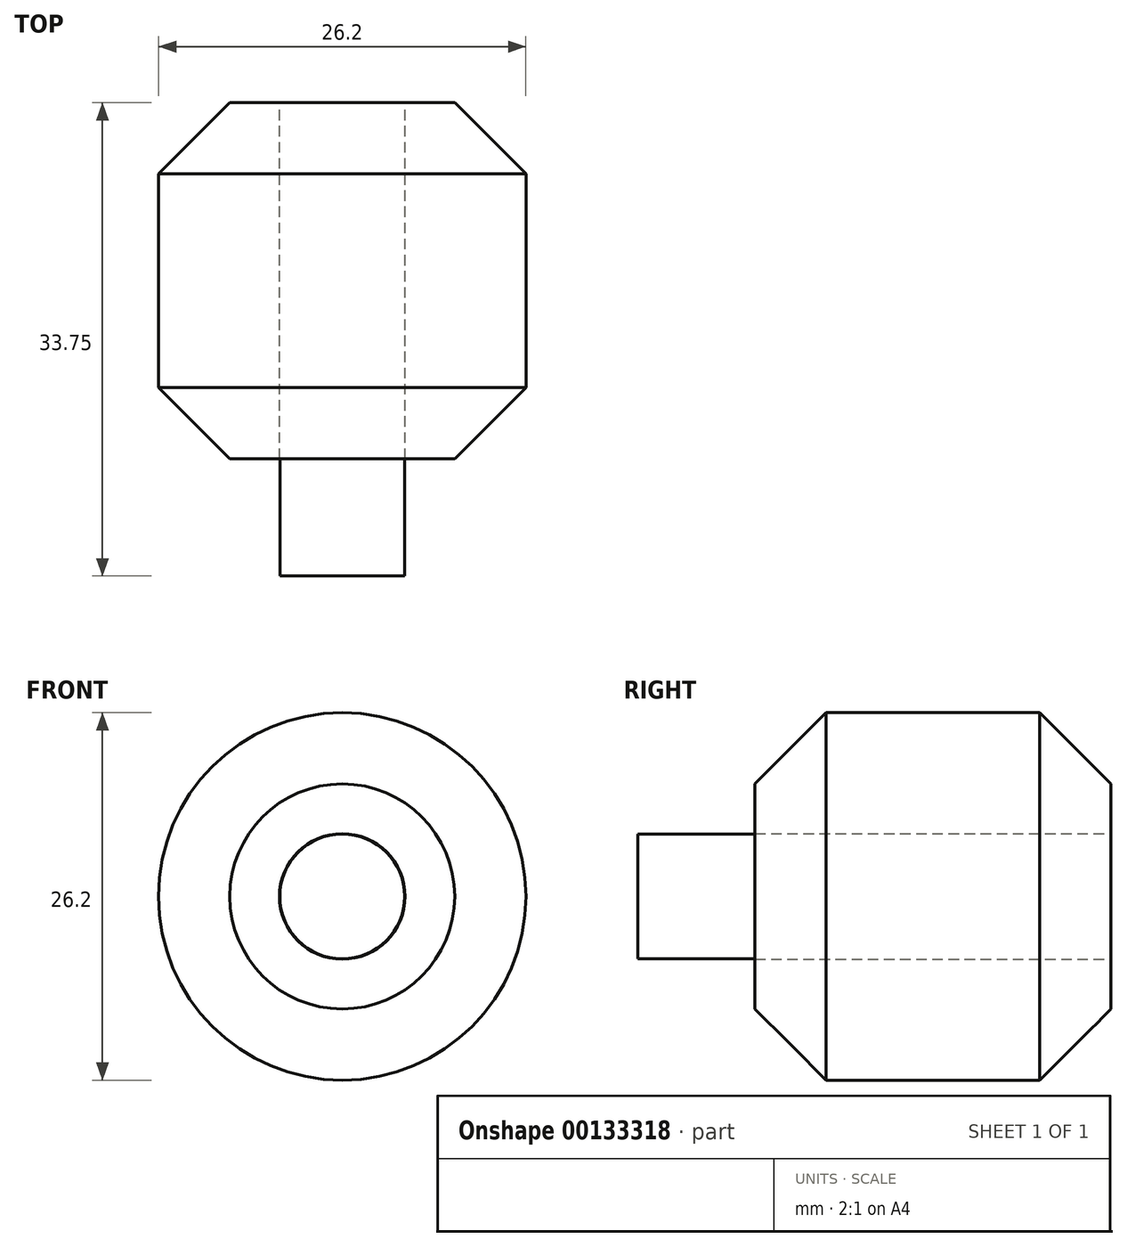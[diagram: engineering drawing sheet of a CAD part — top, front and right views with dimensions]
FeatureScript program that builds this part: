
annotation { "Feature Type Name" : "Feature", "Feature Type Description" : "" }
export const myFeature = defineFeature(function(context is Context, id is Id, definition is map)
    precondition{}
    {
        {
            var Q0;
            Q0=qCreatedBy(makeId("Front.planeOp"),FACE);
            var sketch = newSketch(context, id + "F0", { "sketchPlane" : qUnion([Q0])});
            skCircle(sketch, "E0", {"center": v(0, 0) * mm, "radius": 13.1 * mm});
            skCircle(sketch, "E1", {"center": v(0, 0) * mm, "radius": 4.48 * mm});
            skSolve(sketch);
        }
        {
            var Q0;
            Q0 = qSketchRegion(id + "F0", true);
            extrude(context, id + "F1", {"entities" : qUnion([Q0]), "depth" : 25.4 * mm});
        }
        {
            var Q0;
            Q0=makeQuery(id+"F1.opExtrude","CAP_FACE",FACE,{"disambiguationData":[OSD([sQuery(id+"F0.wireOp",EDGE,"E0"),sQuery(id+"F0.wireOp",EDGE,"E1")])],"isStart":false});
            var sketch = newSketch(context, id + "F2", { "sketchPlane" : qUnion([Q0])});
            skCircle(sketch, "E2", {"center": v(0, 0) * mm, "radius": 4.45 * mm});
            skSolve(sketch);
        }
        {
            var Q0;
            Q0 = qSketchRegion(id + "F2", true);
            extrude(context, id + "F3", {"entities" : qUnion([Q0]), "depth" : 8.35 * mm});
        }
        {
            var Q0;
            Q0=makeQuery(id+"F1.opExtrude","CAP_EDGE",EDGE,{"disambiguationData":[OSD([sQuery(id+"F0.wireOp",EDGE,"E0")])],"isStart":false});
            chamfer(context, id + "F4", {"entities" : qUnion([Q0]), "width" : 5.08 * mm, "tangentPropagation" : true});
        }
        {
            var Q0;
            Q0=makeQuery(id+"F1.opExtrude","CAP_EDGE",EDGE,{"disambiguationData":[OSD([sQuery(id+"F0.wireOp",EDGE,"E0")])],"isStart":true});
            chamfer(context, id + "F5", {"entities" : qUnion([Q0]), "width" : 5.08 * mm, "tangentPropagation" : true});
        }
    });
